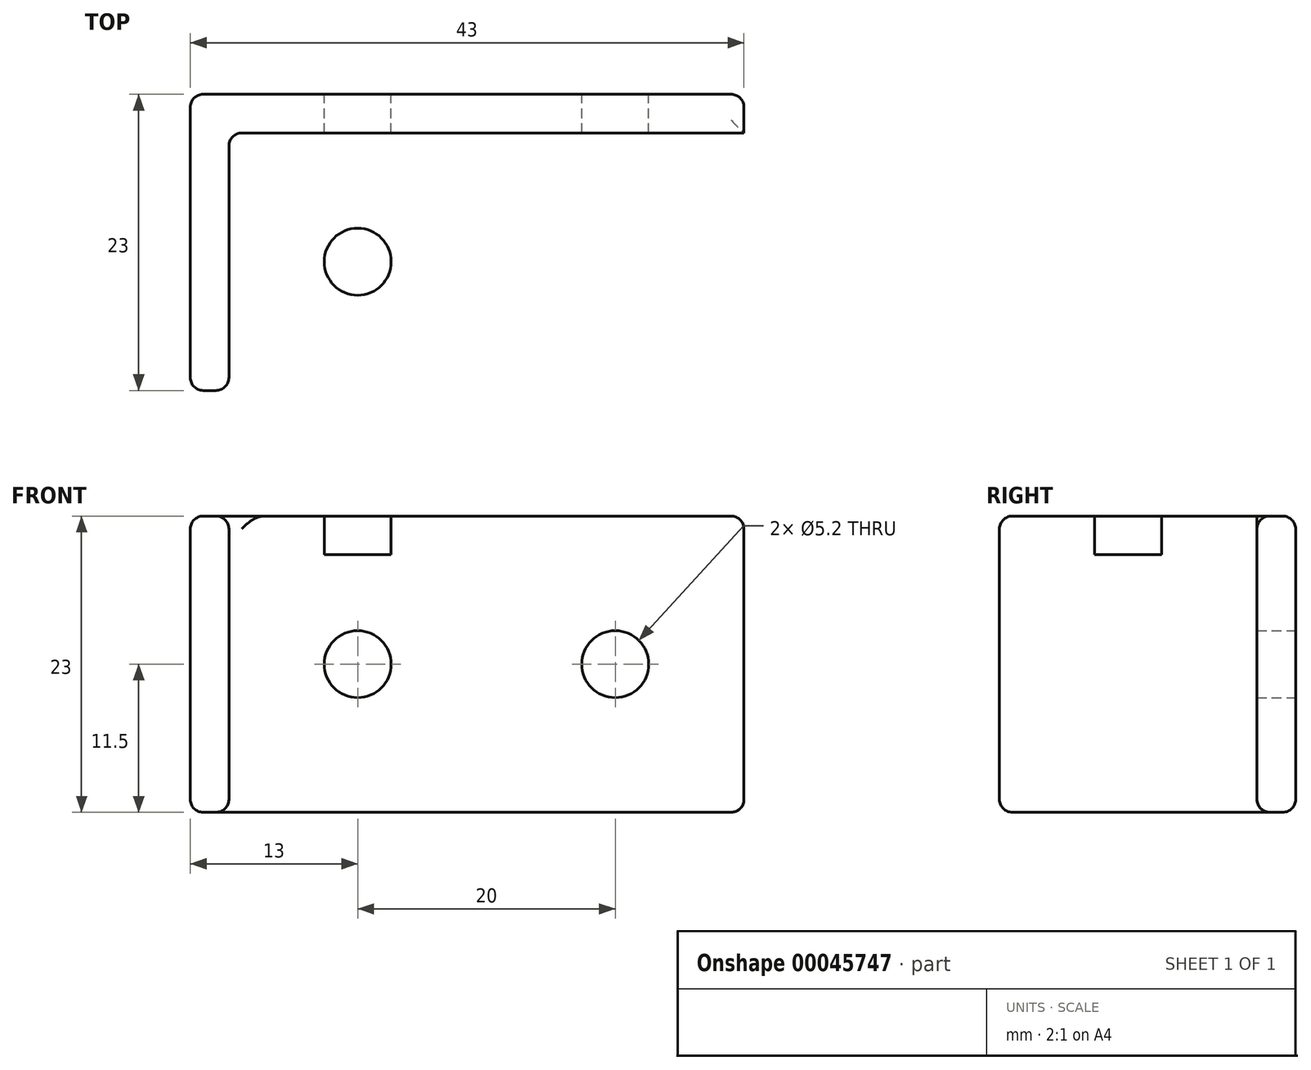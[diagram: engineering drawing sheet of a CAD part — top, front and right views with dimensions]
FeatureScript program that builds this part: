
annotation { "Feature Type Name" : "Feature", "Feature Type Description" : "" }
export const myFeature = defineFeature(function(context is Context, id is Id, definition is map)
    precondition{}
    {
        {
            var Q0;
            Q0=qCreatedBy(makeId("Front.planeOp"),FACE);
            var sketch = newSketch(context, id + "F0", { "sketchPlane" : qUnion([Q0])});
            skLineSegment(sketch, "E0.rect.bottom", {"start": v(21.5, 11.5) * mm, "end": v(-21.5, 11.5) * mm});
            skLineSegment(sketch, "E0.rect.top", {"start": v(21.5, -11.5) * mm, "end": v(-21.5, -11.5) * mm});
            skLineSegment(sketch, "E0.rect.left", {"start": v(21.5, 11.5) * mm, "end": v(21.5, -11.5) * mm});
            skLineSegment(sketch, "E0.rect.right", {"start": v(-21.5, 11.5) * mm, "end": v(-21.5, -11.5) * mm});
            skPoint(sketch, "E0.rect.middle", {"position": v(0, 0) * mm});
            skCircle(sketch, "E1", {"center": v(-11.5, 0) * mm, "radius": 2.6 * mm});
            skCircle(sketch, "E2", {"center": v(8.5, 0) * mm, "radius": 2.6 * mm});
            skSolve(sketch);
        }
        {
            var Q0;
            {var subQ2=sQuery(id+"F0.wireOp",EDGE,"E0.rect.left");Q0=makeQuery(id+"F0.imprint","IMPRINT",FACE,{"disambiguationData":[TD([[makeQuery(id+"F0.imprint","IMPRINT",EDGE,{"derivedFrom":subQ2}),-1.0]])]});}
            extrude(context, id + "F1", {"entities" : qUnion([Q0]), "endBound" : BoundingType.SYMMETRIC, "depth" : 3 * mm});
        }
        {
            var Q0;
            Q0=makeQuery(id+"F1.opExtrude","CAP_FACE",FACE,{"disambiguationData":[OSD([sQuery(id+"F0.wireOp",EDGE,"E0.rect.bottom"),sQuery(id+"F0.wireOp",EDGE,"E0.rect.top"),sQuery(id+"F0.wireOp",EDGE,"E0.rect.left"),sQuery(id+"F0.wireOp",EDGE,"E0.rect.right"),sQuery(id+"F0.wireOp",EDGE,"E1"),sQuery(id+"F0.wireOp",EDGE,"E2")])],"isStart":false});
            var sketch = newSketch(context, id + "F2", { "sketchPlane" : qUnion([Q0])});
            skLineSegment(sketch, "E3.0", {"start": v(21.5, 11.5) * mm, "end": v(-21.5, 11.5) * mm});
            skLineSegment(sketch, "E4.0", {"start": v(21.5, 11.5) * mm, "end": v(21.5, -11.5) * mm});
            skLineSegment(sketch, "E5.0", {"start": v(18.5, 8.5) * mm, "end": v(-21.5, 8.5) * mm});
            skLineSegment(sketch, "E5.1", {"start": v(18.5, 8.5) * mm, "end": v(18.5, -11.5) * mm});
            skLineSegment(sketch, "E6.0", {"start": v(-21.5, 11.5) * mm, "end": v(-21.5, -11.5) * mm});
            skSolve(sketch);
        }
        {
            var Q0;
            {var subQ2=sQuery(id+"F2.wireOp",EDGE,"E3.0");Q0=makeQuery(id+"F2.imprint","IMPRINT",FACE,{"disambiguationData":[TD([[makeQuery(id+"F2.imprint","IMPRINT",EDGE,{"derivedFrom":subQ2}),1.0]])]});}
            extrude(context, id + "F3", {"entities" : qUnion([Q0]), "operationType" : NewBodyOperationType.ADD, "depth" : 20 * mm});
        }
        {
            var Q0;
            Q0=makeQuery(id+"F3.opExtrude","SWEPT_FACE",FACE,{"disambiguationData":[OSD([sQuery(id+"F2.wireOp",EDGE,"E5.0")])]});
            var sketch = newSketch(context, id + "F4", { "sketchPlane" : qUnion([Q0])});
            skLineSegment(sketch, "E7", {"start": v(5.9, -1.5) * mm, "end": v(5.9, 1.5) * mm});
            skLineSegment(sketch, "E8", {"start": v(11.1, 1.5) * mm, "end": v(11.1, -1.5) * mm});
            skLineSegment(sketch, "E9", {"start": v(5.9, 1.5) * mm, "end": v(11.1, 21.5) * mm});
            skCircle(sketch, "E10", {"center": v(8.5, 11.5) * mm, "radius": 2.6 * mm});
            skSolve(sketch);
        }
        {
            var Q0;
            {var subQ0=sQuery(id+"F4.wireOp",EDGE,"E10");var subQ1=sQuery(id+"F4.wireOp",EDGE,"E9");var subQ3=makeQuery(id+"F4.imprint","INTERSECT",VERTEX,{"disambiguationData":[OD(0.0)],"derivedFrom":[subQ1,subQ0]});Q0=makeQuery(id+"F4.imprint","IMPRINT",FACE,{"disambiguationData":[TD([[makeQuery(id+"F4.imprint","IMPRINT",EDGE,{"disambiguationData":[TD([[subQ3,-1.0]])],"derivedFrom":subQ1}),1.0]])]});}
            var Q1;
            {var subQ0=sQuery(id+"F4.wireOp",EDGE,"E10");var subQ1=sQuery(id+"F4.wireOp",EDGE,"E9");var subQ3=makeQuery(id+"F4.imprint","INTERSECT",VERTEX,{"disambiguationData":[OD(0.0)],"derivedFrom":[subQ1,subQ0]});Q1=makeQuery(id+"F4.imprint","IMPRINT",FACE,{"disambiguationData":[TD([[makeQuery(id+"F4.imprint","IMPRINT",EDGE,{"disambiguationData":[TD([[subQ3,-1.0]])],"derivedFrom":subQ1}),-1.0]])]});}
            extrude(context, id + "F5", {"entities" : qUnion([Q0, Q1]), "operationType" : NewBodyOperationType.REMOVE, "endBound" : BoundingType.THROUGH_ALL, "oppositeDirection" : true, "depth" : 25.4 * mm});
        }
        {
            var Q0;
            Q0=makeQuery(id+"F3.opExtrude","SWEPT_FACE",FACE,{"disambiguationData":[OSD([sQuery(id+"F2.wireOp",EDGE,"E5.0")])]});
            var sketch = newSketch(context, id + "F6", { "sketchPlane" : qUnion([Q0])});
            skLineSegment(sketch, "E11.0", {"start": v(18.5, 21.5) * mm, "end": v(-21.5, 21.5) * mm});
            skLineSegment(sketch, "E12.0", {"start": v(-21.5, 21.5) * mm, "end": v(-21.5, 1.5) * mm});
            skLineSegment(sketch, "E13", {"start": v(-21.5, 3.5) * mm, "end": v(3.5, 21.5) * mm});
            skSolve(sketch);
        }
        {
            var Q0;
            {var subQ0=sQuery(id+"F6.wireOp",EDGE,"E13");Q0=makeQuery(id+"F6.imprint","IMPRINT",FACE,{"disambiguationData":[TD([[makeQuery(id+"F6.imprint","IMPRINT",EDGE,{"derivedFrom":subQ0}),1.0]])]});}
            extrude(context, id + "F7", {"entities" : qUnion([Q0]), "operationType" : NewBodyOperationType.REMOVE, "endBound" : BoundingType.THROUGH_ALL, "oppositeDirection" : true, "depth" : 25.4 * mm});
        }
        {
            var Q0;
            Q0=makeQuery(id+"F3.boolean.opBoolean","MERGE",FACE,{"derivedFrom":[makeQuery(id+"F1.opExtrude","SWEPT_FACE",FACE,{"disambiguationData":[OSD([sQuery(id+"F0.wireOp",EDGE,"E0.rect.left")])]}),makeQuery(id+"F3.opExtrude","SWEPT_FACE",FACE,{"disambiguationData":[OSD([sQuery(id+"F2.wireOp",EDGE,"E4.0")])]})]});
            var Q1;
            Q1=makeQuery(id+"F1.opExtrude","CAP_EDGE",EDGE,{"disambiguationData":[OSD([sQuery(id+"F0.wireOp",EDGE,"E0.rect.top")])],"isStart":true});
            var Q2;
            Q2=makeQuery(id+"F1.opExtrude","CAP_EDGE",EDGE,{"disambiguationData":[OSD([sQuery(id+"F0.wireOp",EDGE,"E0.rect.bottom")])],"isStart":true});
            var Q3;
            Q3=makeQuery(id+"F3.boolean.opBoolean","MERGE",EDGE,{"derivedFrom":[makeQuery(id+"F1.opExtrude","SWEPT_EDGE",EDGE,{"disambiguationData":[OSD([sQuery(id+"F0.wireOp",EDGE,"E0.rect.bottom"),sQuery(id+"F0.wireOp",EDGE,"E0.rect.right")])]}),makeQuery(id+"F3.opExtrude","SWEPT_EDGE",EDGE,{"disambiguationData":[OSD([sQuery(id+"F2.wireOp",EDGE,"E3.0"),sQuery(id+"F2.wireOp",EDGE,"E6.0")])]})]});
            var Q4;
            Q4=makeQuery(id+"F7.boolean.opBoolean","INTERSECT",EDGE,{"derivedFrom":[makeQuery(id+"F3.boolean.opBoolean","MERGE",FACE,{"derivedFrom":[makeQuery(id+"F1.opExtrude","SWEPT_FACE",FACE,{"disambiguationData":[OSD([sQuery(id+"F0.wireOp",EDGE,"E0.rect.bottom")])]}),makeQuery(id+"F3.opExtrude","SWEPT_FACE",FACE,{"disambiguationData":[OSD([sQuery(id+"F2.wireOp",EDGE,"E3.0")])]})]}),makeQuery(id+"F7.opExtrude","SWEPT_FACE",FACE,{"disambiguationData":[OSD([sQuery(id+"F6.wireOp",EDGE,"E13")])]})]});
            var Q5;
            Q5=makeQuery(id+"F3.opExtrude","CAP_EDGE",EDGE,{"disambiguationData":[OSD([sQuery(id+"F2.wireOp",EDGE,"E3.0")])],"isStart":false});
            var Q6;
            Q6=makeQuery(id+"F7.boolean.opBoolean","COPY",EDGE,{"derivedFrom":makeQuery(id+"F7.opExtrude","CAP_EDGE",EDGE,{"disambiguationData":[OSD([sQuery(id+"F6.wireOp",EDGE,"E13")])],"isStart":true})});
            var Q7;
            Q7=makeQuery(id+"F7.boolean.opBoolean","COPY",EDGE,{"derivedFrom":makeQuery(id+"F7.opExtrude","SWEPT_EDGE",EDGE,{"disambiguationData":[OSD([sQuery(id+"F6.wireOp",EDGE,"E11.0"),sQuery(id+"F6.wireOp",EDGE,"E13")])]})});
            var Q8;
            Q8=makeQuery(id+"F3.opExtrude","CAP_EDGE",EDGE,{"disambiguationData":[OSD([sQuery(id+"F2.wireOp",EDGE,"E5.0")])],"isStart":false});
            var Q9;
            Q9=makeQuery(id+"F3.opExtrude","CAP_EDGE",EDGE,{"disambiguationData":[OSD([sQuery(id+"F2.wireOp",EDGE,"E5.1")])],"isStart":false});
            var Q10;
            Q10=makeQuery(id+"F1.opExtrude","CAP_EDGE",EDGE,{"disambiguationData":[OSD([sQuery(id+"F0.wireOp",EDGE,"E0.rect.top")])],"isStart":false});
            var Q11;
            Q11=makeQuery(id+"F3.opExtrude","SWEPT_FACE",FACE,{"disambiguationData":[OSD([sQuery(id+"F2.wireOp",EDGE,"E5.1")])]});
            var Q12;
            {var subQ0=sQuery(id+"F0.wireOp",EDGE,"E0.rect.top");Q12=makeQuery(id+"F3.boolean.opBoolean","MERGE",FACE,{"derivedFrom":[makeQuery(id+"F1.opExtrude","SWEPT_FACE",FACE,{"disambiguationData":[OSD([subQ0])]}),makeQuery(id+"F3.opExtrude","SWEPT_FACE",FACE,{"disambiguationData":[OSD([subQ0])]})]});}
            var Q13;
            Q13=makeQuery(id+"F1.opExtrude","CAP_EDGE",EDGE,{"disambiguationData":[OSD([sQuery(id+"F0.wireOp",EDGE,"E0.rect.right")])],"isStart":true});
            var Q14;
            Q14=makeQuery(id+"F1.opExtrude","CAP_EDGE",EDGE,{"disambiguationData":[OSD([sQuery(id+"F0.wireOp",EDGE,"E0.rect.right")])],"isStart":false});
            var Q15;
            Q15=makeQuery(id+"F3.opExtrude","SWEPT_EDGE",EDGE,{"disambiguationData":[OSD([sQuery(id+"F2.wireOp",EDGE,"E5.0"),sQuery(id+"F2.wireOp",EDGE,"E6.0")])]});
            var Q16;
            Q16=makeQuery(id+"F7.boolean.opBoolean","COPY",EDGE,{"derivedFrom":makeQuery(id+"F7.opExtrude","SWEPT_EDGE",EDGE,{"disambiguationData":[OSD([sQuery(id+"F6.wireOp",EDGE,"E12.0"),sQuery(id+"F6.wireOp",EDGE,"E13")])]})});
            var Q17;
            Q17=makeQuery(id+"F3.opExtrude","CAP_EDGE",EDGE,{"disambiguationData":[OSD([sQuery(id+"F2.wireOp",EDGE,"E5.0")])],"isStart":true});
            fillet(context, id + "F8", {"entities" : qUnion([Q0, Q1, Q2, Q3, Q4, Q5, Q6, Q7, Q8, Q9, Q10, Q11, Q12, Q13, Q14, Q15, Q16, Q17]), "radius" : 1 * mm, "allowEdgeOverflow" : false});
        }
        {
            var Q0;
            Q0=makeQuery(id+"F1.opExtrude","SWEPT_BODY",BODY,{"disambiguationData":[OSD([sQuery(id+"F0.wireOp",EDGE,"E0.rect.bottom"),sQuery(id+"F0.wireOp",EDGE,"E0.rect.top"),sQuery(id+"F0.wireOp",EDGE,"E0.rect.left"),sQuery(id+"F0.wireOp",EDGE,"E0.rect.right"),sQuery(id+"F0.wireOp",EDGE,"E1"),sQuery(id+"F0.wireOp",EDGE,"E2")])]});
            var Q1;
            Q1=makeQuery(id+"F3.boolean.opBoolean","MERGE",FACE,{"derivedFrom":[makeQuery(id+"F1.opExtrude","SWEPT_FACE",FACE,{"disambiguationData":[OSD([sQuery(id+"F0.wireOp",EDGE,"E0.rect.right")])]}),makeQuery(id+"F3.opExtrude","SWEPT_FACE",FACE,{"disambiguationData":[OSD([sQuery(id+"F2.wireOp",EDGE,"E6.0")])]})]});
            mirror(context, id + "F10", {"entities" : qUnion([Q0]), "mirrorPlane" : qUnion([Q1])});
        }
        {
            var Q0;
            Q0=makeQuery(id+"F1.opExtrude","SWEPT_BODY",BODY,{"disambiguationData":[OSD([sQuery(id+"F0.wireOp",EDGE,"E0.rect.bottom"),sQuery(id+"F0.wireOp",EDGE,"E0.rect.top"),sQuery(id+"F0.wireOp",EDGE,"E0.rect.left"),sQuery(id+"F0.wireOp",EDGE,"E0.rect.right"),sQuery(id+"F0.wireOp",EDGE,"E1"),sQuery(id+"F0.wireOp",EDGE,"E2")])]});
            deleteBodies(context, id + "F9", {"entities" : qUnion([Q0])});
        }
    });
